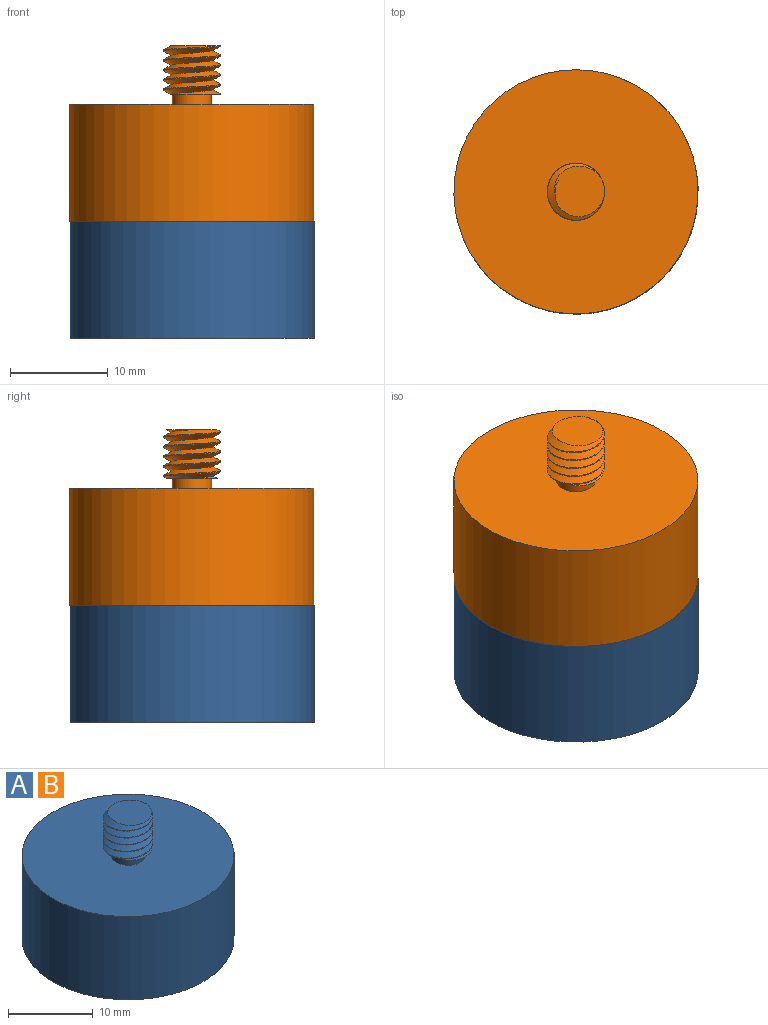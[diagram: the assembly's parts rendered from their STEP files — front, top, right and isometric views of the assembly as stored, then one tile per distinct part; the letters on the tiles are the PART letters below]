
ASSEMBLY  parts=2 mates=1
PART A: 15 faces, bbox 25.6x25.6x19.9 mm
  f0: bspline ~7.75x7.16mm, area 101.6mm2, adj f1,f2,f11,f14
  f1: bspline ~7.75x7.16mm, area 101.6mm2, adj f0,f2,f11,f14
  f2: plane 25.54x25.54mm, normal (0,0,-1), area 463.7mm2, adj f0,f1,f7,f14
  f3: plane 5.78x5.69mm, normal (0,0,-1), area 8.3mm2, adj f5,f6,f9,f10
  f4: plane 5.78x5.69mm, normal (0,0,1), area 21mm2, adj f5,f6,f10
  f5: bspline ~6.93x6.16mm, area 72.4mm2, adj f3,f4,f6,f10
  f6: bspline ~6.93x6.16mm, area 72.5mm2, adj f3,f4,f5,f10
  f7: cylinder r=12.5mm len=25mm, axis (0,0,-1), area 942.5mm2, adj f2,f8
  f8: plane 25x25mm, normal (0,0,1), area 478.2mm2, adj f7,f9
  f9: cylinder r=2.01mm len=4.02mm, axis (0,0,1), area 12.5mm2, adj f3,f8
  f10: cylinder r=2.93mm len=5.86mm, axis (0,0,1), area 8.4mm2, adj f3,f4,f5,f6
  f11: plane 7.52x7.52mm, normal (0,0,1), area 11.1mm2, adj f0,f1,f12,f14
  f12: cylinder r=3.49mm len=6.98mm, axis (0,0,1), area 21.7mm2, adj f11,f13
  f13: plane 6.98x6.98mm, normal (0,0,-1), area 38.3mm2, adj f12
  f14: cylinder r=2.57mm len=6.01mm, axis (0,0,-1), area 9.1mm2, adj f0,f1,f2,f11
PART B: same geometry as A
PLACE A rot(axis=(0,0,1),165deg) t=(6.72,2.38,-12.57)mm
PLACE B rot(axis=(0,0,1),5deg) t=(6.7,2.37,-0.57)mm
MATE revolute B.f2 <-> A.f7  axis (0,0,-1) through (6.72,2.38,-0.57)mm
